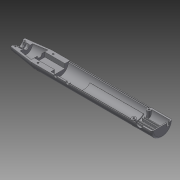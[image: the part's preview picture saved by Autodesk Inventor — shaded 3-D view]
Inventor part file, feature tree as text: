
AUTODESK INVENTOR PART (.ipt)
format: ipt  version: 2014 (Build 180170000, 170)  size: 497,152 bytes
history: native  units: mm
features: extrude x20, sketch x20, other x12, projected_geometry x3, loft x1, fillet x1, mirror x1
ambient origin geometry x8: Origin, YZ Plane, XZ Plane, XY Plane, X Axis, Y Axis, Z Axis, Center Point
bodies: Body1 (feature_tree)
feature tree (58):
  other  "Твердое тело1"
  extrude  "Выдавливание1"  Depth=11.0mm
  other  "РабПлоскость1"
  sketch  "Эскиз3"
  extrude  "Выдавливание2"  Depth=13.0mm
  loft  "Лофт2"
  extrude  "Выдавливание3"  Depth=180.0mm
  extrude  "Выдавливание4"  Depth=9.0mm
  extrude  "Выдавливание_Стойки"  Depth=6.0mm
  other  "РабПлоскость2"
  extrude  "Выдавливание Кнопки"  Depth=1.2mm TaperAngle=0.0deg
  fillet  "Сопряжение Торец копуса"  [1 undecoded]
  other  "РабПлоскость3"
  other  "РабПлоскость8"
  extrude  "Выдавливание8"  TaperAngle=0.0deg  [1 undecoded]
  other  "РабПлоскость7"
  extrude  "Выдавливание9"  Depth=1.5mm
  other  "РабПлоскость6"
  extrude  "Выдавливание11"  Depth=0.8mm
  other  "РабПлоскость5 Середина корпуса"
  extrude  "Выдавливание12"  Depth=1.0mm
  extrude  "Выдавливание13"  Depth=27.0mm TaperAngle=0.0deg
  extrude  "Выдавливание14"  Depth=4.0mm
  extrude  "Выдавливание15"  Depth=3.0mm
  extrude  "Выдавливание16"  Depth=2.0mm TaperAngle=0.0deg
  extrude  "Выдавливание17"  Depth=1.5mm
  extrude  "Выдавливание18"  Depth=5.0mm
  extrude  "Выдавливание19"  Depth=4.0mm
  extrude  "Выдавливание20"  Depth=25.0mm
  extrude  "Выдавливание21"  Depth=120.0mm
  mirror  "Зеркальное отражение1"
  other  "Выступ2"
  other  "Выступ3"
  other  "РабПлоскость9"
  extrude  "Выдавливание22"  Depth=2.0mm
  sketch  "Эскиз1"
  sketch  "Эскиз4"
  other  "Ребра2"
  sketch  "Эскиз5"
  sketch  "Эскиз6"
  sketch  "Эскиз7"
  sketch  "Эскиз8"
  sketch  "Эскиз10"
  sketch  "Эскиз11"
  sketch  "Эскиз14"
  sketch  "Эскиз18"
  sketch  "Эскиз19"
  sketch  "Эскиз20"
  projected_geometry  "Спроецированная петля1"
  sketch  "Эскиз21"
  sketch  "Эскиз22"
  projected_geometry  "Спроецированная петля2"
  sketch  "Эскиз23"
  sketch  "Эскиз24"
  projected_geometry  "Спроецированная петля3"
  sketch  "Эскиз25"
  sketch  "Эскиз26"
  sketch  "Эскиз27"
note: 2 required parameter values undecoded (feature->parameter linkage not recoverable at this tier; creation-order binding heuristic only, values carry confidence <= 0.55)
